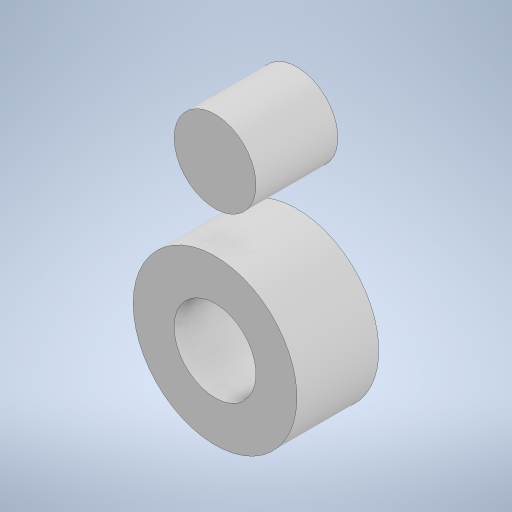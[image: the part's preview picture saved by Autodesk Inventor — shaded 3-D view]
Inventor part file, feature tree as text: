
AUTODESK INVENTOR PART (.ipt)
format: ipt  version: 2024 (Build 280153000, 153)  size: 232,960 bytes
history: native  units: mm
features: extrude x1, sketch x1
ambient origin geometry x8: Origin, YZ Plane, XZ Plane, XY Plane, X Axis, Y Axis, Z Axis, Center Point
bodies: Solid1 (feature_tree)
feature tree (2):
  extrude  "Extrusion1"  Depth=10.0mm
  sketch  "Sketch1"  dims[d0=5.0mm d1=10.0mm d2=5.0mm d3=10.0mm d4=5.0mm d5=0.0mm]
